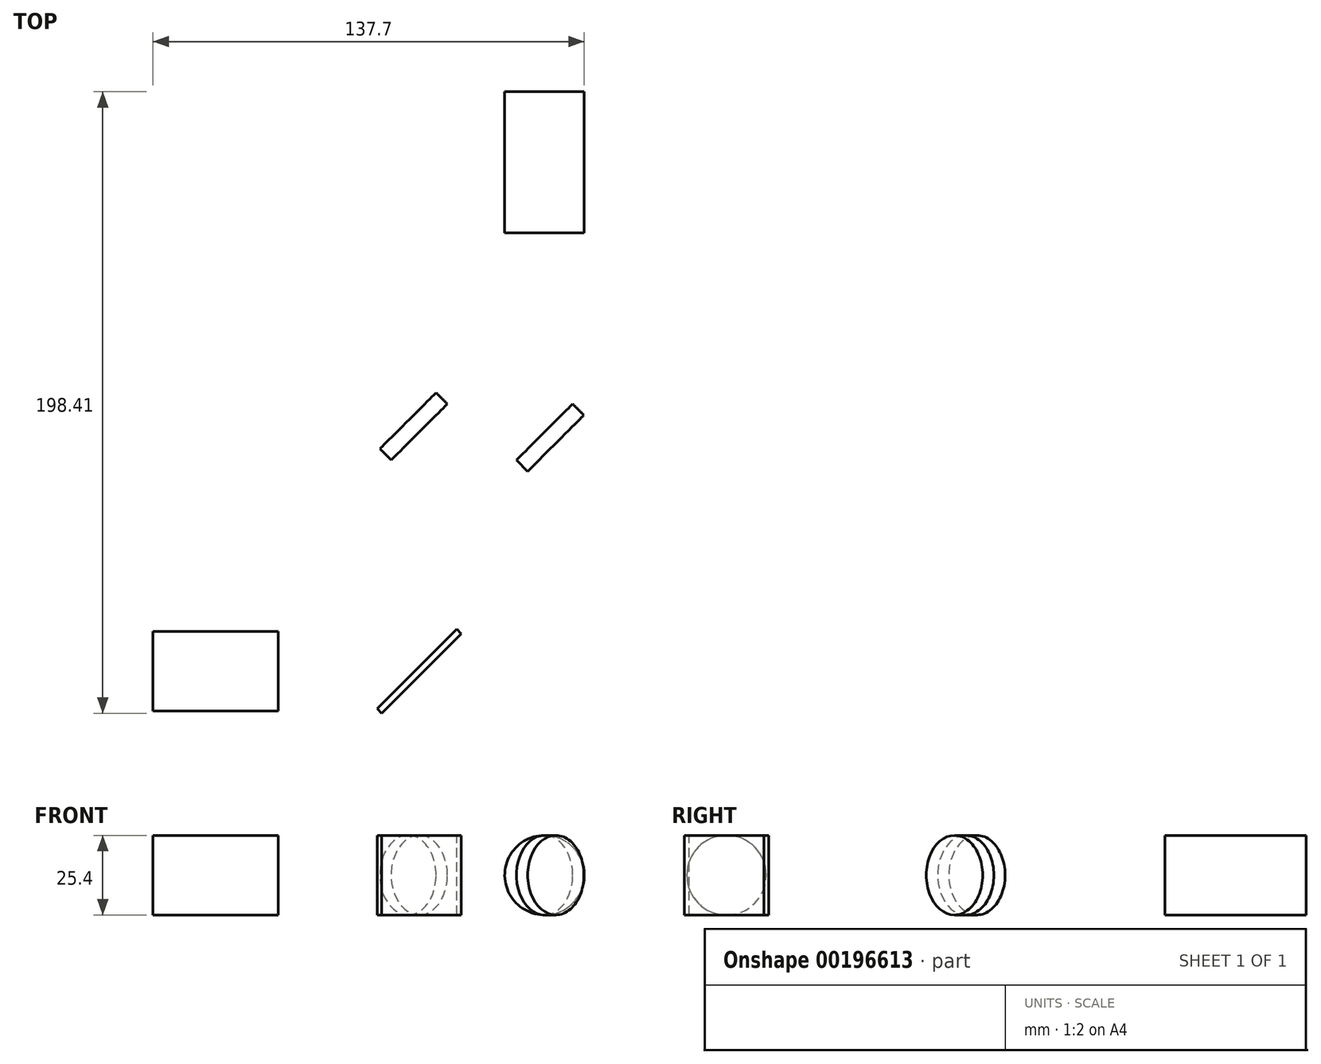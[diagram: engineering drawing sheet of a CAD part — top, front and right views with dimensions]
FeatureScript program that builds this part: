
annotation { "Feature Type Name" : "Feature", "Feature Type Description" : "" }
export const myFeature = defineFeature(function(context is Context, id is Id, definition is map)
    precondition{}
    {
        {
            var Q0;
            Q0=qCreatedBy(makeId("Top.planeOp"),FACE);
            var sketch = newSketch(context, id + "F0", { "sketchPlane" : qUnion([Q0])});
            skLineSegment(sketch, "E0.bottom", {"start": v(-12.7, 0) * mm, "end": v(12.7, 0) * mm});
            skLineSegment(sketch, "E0.top", {"start": v(-12.7, 45) * mm, "end": v(12.7, 45) * mm});
            skLineSegment(sketch, "E0.left", {"start": v(-12.7, 0) * mm, "end": v(-12.7, 45) * mm});
            skLineSegment(sketch, "E0.right", {"start": v(12.7, 0) * mm, "end": v(12.7, 45) * mm});
            skLineSegment(sketch, "E1", {"start": v(0, 0) * mm, "end": v(-40, 0) * mm, "construction": true});
            skLineSegment(sketch, "E2", {"start": v(-40, 0) * mm, "end": v(-40, -140) * mm, "construction": true});
            skLineSegment(sketch, "E3", {"start": v(-48.98, -148.98) * mm, "end": v(-31.02, -131.02) * mm});
            skLineSegment(sketch, "E4", {"start": v(-40, -140) * mm, "end": v(-85, -140) * mm, "construction": true});
            skLineSegment(sketch, "E5.bottom", {"start": v(-85, -152.7) * mm, "end": v(-125, -152.7) * mm});
            skLineSegment(sketch, "E5.top", {"start": v(-85, -127.3) * mm, "end": v(-125, -127.3) * mm});
            skLineSegment(sketch, "E5.left", {"start": v(-85, -152.7) * mm, "end": v(-85, -127.3) * mm});
            skLineSegment(sketch, "E5.right", {"start": v(-125, -152.7) * mm, "end": v(-125, -127.3) * mm});
            skLineSegment(sketch, "E6", {"start": v(0, 76.85) * mm, "end": v(0, -63.64) * mm, "construction": true});
            skLineSegment(sketch, "E7", {"start": v(-8.98, -72.62) * mm, "end": v(8.98, -54.66) * mm});
            skLineSegment(sketch, "E8", {"start": v(0, -63.64) * mm, "end": v(-40, -63.64) * mm, "construction": true});
            skLineSegment(sketch, "E9", {"start": v(-48.98, -72.62) * mm, "end": v(-31.02, -54.66) * mm});
            skLineSegment(sketch, "E10", {"start": v(-40, -140) * mm, "end": v(20, -140) * mm, "construction": true});
            skSolve(sketch);
        }
        {
            var Q0;
            Q0=sQuery(id+"F0.wireOp",EDGE,"E7");
            cPlane(context, id + "F1", {"entities" : qUnion([Q0]), "cplaneType" : CPlaneType.LINE_ANGLE, "offset" : 0 * mm, "angle" : 90 * degree, "width" : 152.4 * mm, "height" : 152.4 * mm});
        }
        {
            var Q0;
            Q0=qCreatedBy(id+"F1.planeOp",FACE);
            var sketch = newSketch(context, id + "F2", { "sketchPlane" : qUnion([Q0])});
            skCircle(sketch, "E11", {"center": v(-45, 0) * mm, "radius": 12.7 * mm});
            skSolve(sketch);
        }
        {
            var Q0;
            Q0 = qSketchRegion(id + "F2", true);
            extrude(context, id + "F3", {"entities" : qUnion([Q0]), "depth" : 5.08 * mm});
        }
        {
            var Q0;
            Q0=sQuery(id+"F0.wireOp",EDGE,"E9");
            cPlane(context, id + "F4", {"entities" : qUnion([Q0]), "cplaneType" : CPlaneType.LINE_ANGLE, "offset" : 25.4 * mm, "angle" : 90 * degree, "width" : 152.4 * mm, "height" : 152.4 * mm});
        }
        {
            var Q0;
            Q0=qCreatedBy(id+"F4.planeOp",FACE);
            var sketch = newSketch(context, id + "F5", { "sketchPlane" : qUnion([Q0])});
            skCircle(sketch, "E12", {"center": v(-73.28, 0) * mm, "radius": 12.7 * mm});
            skSolve(sketch);
        }
        {
            var Q0;
            Q0 = qSketchRegion(id + "F5", true);
            extrude(context, id + "F6", {"entities" : qUnion([Q0]), "oppositeDirection" : true, "depth" : 5.08 * mm});
        }
        {
            var Q0;
            Q0=sQuery(id+"F0.wireOp",EDGE,"E3");
            cPlane(context, id + "F7", {"entities" : qUnion([Q0]), "cplaneType" : CPlaneType.LINE_ANGLE, "offset" : 25.4 * mm, "angle" : 90 * degree, "width" : 152.4 * mm, "height" : 152.4 * mm});
        }
        {
            var Q0;
            Q0=qCreatedBy(id+"F7.planeOp",FACE);
            var sketch = newSketch(context, id + "F8", { "sketchPlane" : qUnion([Q0])});
            skLineSegment(sketch, "E13.bottom", {"start": v(-109.32, -12.7) * mm, "end": v(-145.24, -12.7) * mm});
            skLineSegment(sketch, "E13.top", {"start": v(-109.32, 12.7) * mm, "end": v(-145.24, 12.7) * mm});
            skLineSegment(sketch, "E13.left", {"start": v(-109.32, -12.7) * mm, "end": v(-109.32, 12.7) * mm});
            skLineSegment(sketch, "E13.right", {"start": v(-145.24, -12.7) * mm, "end": v(-145.24, 12.7) * mm});
            skPoint(sketch, "E13.middle", {"position": v(-127.28, 0) * mm});
            skSolve(sketch);
        }
        {
            var Q0;
            Q0 = qSketchRegion(id + "F8", true);
            extrude(context, id + "F9", {"entities" : qUnion([Q0]), "endBound" : BoundingType.SYMMETRIC, "depth" : 2 * mm});
        }
        {
            var Q0;
            Q0=sQuery(id+"F0.wireOp",EDGE,"E0.bottom");
            cPlane(context, id + "F10", {"entities" : qUnion([Q0]), "cplaneType" : CPlaneType.LINE_ANGLE, "offset" : 25.4 * mm, "angle" : 0 * degree, "width" : 152.4 * mm, "height" : 152.4 * mm});
        }
        {
            var Q0;
            Q0=qCreatedBy(id+"F10.planeOp",FACE);
            var sketch = newSketch(context, id + "F11", { "sketchPlane" : qUnion([Q0])});
            skCircle(sketch, "E14", {"center": v(0, 0) * mm, "radius": 12.7 * mm});
            skSolve(sketch);
        }
        {
            var Q0;
            Q0 = qSketchRegion(id + "F11", true);
            var Q1;
            Q1=sQuery(id+"F0.wireOp",VERTEX,"E0.right.end");
            extrude(context, id + "F12", {"entities" : qUnion([Q0]), "endBound" : BoundingType.UP_TO_VERTEX, "endBoundEntityVertex" : qUnion([Q1]), "depth" : 25.4 * mm});
        }
        {
            var Q0;
            Q0=sQuery(id+"F0.wireOp",EDGE,"E5.left");
            cPlane(context, id + "F13", {"entities" : qUnion([Q0]), "cplaneType" : CPlaneType.LINE_ANGLE, "offset" : 25.4 * mm, "angle" : 90 * degree, "width" : 152.4 * mm, "height" : 152.4 * mm});
        }
        {
            var Q0;
            Q0=qCreatedBy(id+"F13.planeOp",FACE);
            var sketch = newSketch(context, id + "F14", { "sketchPlane" : qUnion([Q0])});
            skCircle(sketch, "E15", {"center": v(-140, 0) * mm, "radius": 12.7 * mm});
            skSolve(sketch);
        }
        {
            var Q0;
            Q0 = qSketchRegion(id + "F14", true);
            var Q1;
            Q1=sQuery(id+"F0.wireOp",VERTEX,"E5.right.end");
            extrude(context, id + "F15", {"entities" : qUnion([Q0]), "endBound" : BoundingType.UP_TO_VERTEX, "oppositeDirection" : true, "endBoundEntityVertex" : qUnion([Q1]), "depth" : 25.4 * mm});
        }
    });
